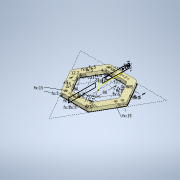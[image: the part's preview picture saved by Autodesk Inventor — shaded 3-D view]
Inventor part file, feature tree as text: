
AUTODESK INVENTOR PART (.ipt)
format: ipt  version: 2021 (Build 250183000, 183)  size: 454,144 bytes
history: native  units: mm
features: sketch x7, extrude x6, projected_geometry x4, fillet x1, pattern_circular x1
ambient origin geometry x8: Origin, YZ Plane, XZ Plane, XY Plane, X Axis, Y Axis, Z Axis, Center Point
bodies: Body1 (feature_tree)
feature tree (19):
  sketch  "스케치1"
  extrude  "돌출18"  Depth=12.7mm
  extrude  "돌출20"  Depth=80.0mm
  fillet  "모깎기4"  Radius=5.3mm
  extrude  "돌출23"  Depth=5.0mm
  pattern_circular  "원형 패턴5"  Count=2  [1 undecoded]
  sketch  "스케치25"
  extrude  "돌출30"  Depth=5.0mm
  extrude  "돌출31"  Depth=20.0mm
  extrude  "돌출32"  Depth=5.0mm
  sketch  "스케치15"
  projected_geometry  "투영된 루프10"
  sketch  "스케치18"
  projected_geometry  "투영된 루프13"
  sketch  "스케치26"
  projected_geometry  "투영된 루프19"
  sketch  "스케치27"
  sketch  "스케치28"
  projected_geometry  "투영된 루프20"
note: 1 required parameter value undecoded (feature->parameter linkage not recoverable at this tier; creation-order binding heuristic only, values carry confidence <= 0.55)
